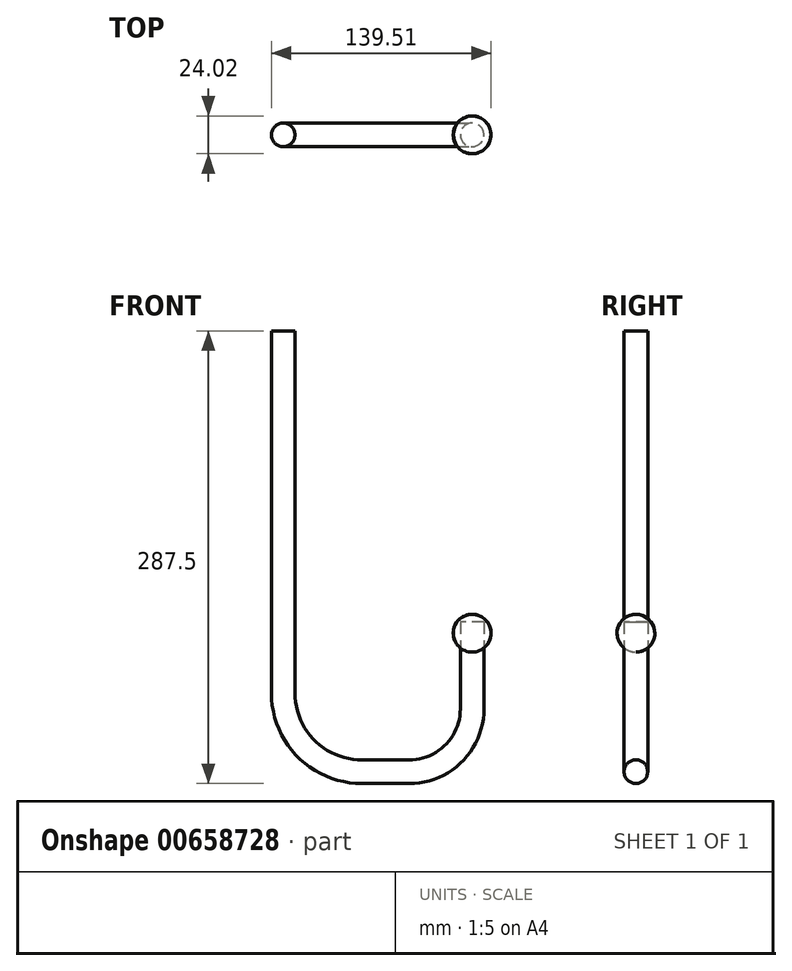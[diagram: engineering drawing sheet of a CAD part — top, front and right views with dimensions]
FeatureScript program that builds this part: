
annotation { "Feature Type Name" : "Feature", "Feature Type Description" : "" }
export const myFeature = defineFeature(function(context is Context, id is Id, definition is map)
    precondition{}
    {
        {
            var Q0;
            Q0=qCreatedBy(makeId("Front.planeOp"),FACE);
            var sketch = newSketch(context, id + "F0", { "sketchPlane" : qUnion([Q0])});
            skLineSegment(sketch, "E0", {"start": v(0, 50) * mm, "end": v(0, 280) * mm});
            skLineSegment(sketch, "E1", {"start": v(50, 0) * mm, "end": v(80, 0) * mm});
            skLineSegment(sketch, "E2", {"start": v(120, 40) * mm, "end": v(120, 95) * mm});
            skPoint(sketch, "E3.visualSharp", {"position": v(120, 0) * mm});
            skArc(sketch, "E3.filletArc", {"start": v(80, 0) * mm, "mid": v(108.28, 11.72) * mm, "end": v(120, 40) * mm});
            skPoint(sketch, "E4.visualSharp", {"position": v(0, 0) * mm});
            skArc(sketch, "E4.filletArc", {"start": v(0, 50) * mm, "mid": v(14.64, 14.64) * mm, "end": v(50, 0) * mm});
            skSolve(sketch);
        }
        {
            var Q0;
            Q0=sQuery(id+"F0.wireOp",VERTEX,"E2.end");
            var Q1;
            Q1=qCreatedBy(makeId("Top.planeOp"),FACE);
            cPlane(context, id + "F1", {"entities" : qUnion([Q0, Q1]), "cplaneType" : CPlaneType.PLANE_POINT, "offset" : 25 * mm, "width" : 150 * mm, "height" : 150 * mm});
        }
        {
            var Q0;
            Q0=qCreatedBy(id+"F1.planeOp",FACE);
            var sketch = newSketch(context, id + "F2", { "sketchPlane" : qUnion([Q0])});
            skPoint(sketch, "E5.0", {"position": v(120, 0) * mm});
            skCircle(sketch, "E6", {"center": v(120, 0) * mm, "radius": 7.5 * mm});
            skSolve(sketch);
        }
        {
            var Q0;
            Q0=makeQuery(id+"F2.imprint","IMPRINT",FACE,{"disambiguationData":[TD([[makeQuery(id+"F2.imprint","IMPRINT",EDGE,{"derivedFrom":sQuery(id+"F2.wireOp",EDGE,"E6")}),1.0]])]});
            var Q1;
            Q1=sQuery(id+"F2.wireOp",EDGE,"E6");
            var Q2;
            Q2=sQuery(id+"F0.wireOp",EDGE,"E2");
            var Q3;
            Q3=sQuery(id+"F0.wireOp",EDGE,"E3.filletArc");
            var Q4;
            Q4=sQuery(id+"F0.wireOp",EDGE,"E1");
            var Q5;
            Q5=sQuery(id+"F0.wireOp",EDGE,"E4.filletArc");
            var Q6;
            Q6=sQuery(id+"F0.wireOp",EDGE,"E0");
            sweep(context, id + "F3", {"profiles" : qUnion([Q0]), "surfaceProfiles" : qUnion([Q1]), "path" : qUnion([Q2, Q3, Q4, Q5, Q6])});
        }
        {
            var Q0;
            Q0=sQuery(id+"F0.wireOp",EDGE,"E2");
            cPlane(context, id + "F4", {"entities" : qUnion([Q0]), "cplaneType" : CPlaneType.LINE_ANGLE, "offset" : 25 * mm, "angle" : 0 * degree, "width" : 150 * mm, "height" : 150 * mm});
        }
        {
            var Q0;
            Q0=qCreatedBy(id+"F4.planeOp",FACE);
            var sketch = newSketch(context, id + "F5", { "sketchPlane" : qUnion([Q0])});
            skPoint(sketch, "E7.0", {"position": v(0, 95) * mm});
            skArc(sketch, "E8", {"start": v(0, 71) * mm, "mid": v(12.01, 83) * mm, "end": v(0, 95) * mm});
            skLineSegment(sketch, "E9", {"start": v(0, 71) * mm, "end": v(0, 95) * mm});
            skSolve(sketch);
        }
        {
            var Q0;
            Q0 = qSketchRegion(id + "F5", true);
            var Q1;
            Q1=sQuery(id+"F0.wireOp",EDGE,"E2");
            revolve(context, id + "F6", {"entities" : qUnion([Q0]), "axis" : qUnion([Q1]), "revolveType" : RevolveType.FULL});
        }
        {
            var Q0;
            Q0=makeQuery(id+"F6.opRevolve","SWEPT_BODY",BODY,{"disambiguationData":[OSD([sQuery(id+"F5.wireOp",EDGE,"E8"),sQuery(id+"F5.wireOp",EDGE,"E9")])]});
            var Q1;
            Q1=makeQuery(id+"F3.opSweep","CAP_FACE",FACE,{"disambiguationData":[OSD([sQuery(id+"F0.wireOp",VERTEX,"E2.end"),sQuery(id+"F2.wireOp",EDGE,"E6")])],"isStart":true});
            transform(context, id + "F7", {"entities" : qUnion([Q0]), "transformType" : TransformType.TRANSLATION_DISTANCE, "transformDirection" : qUnion([Q1]), "distance" : 5 * mm, "makeCopy" : false});
        }
    });
